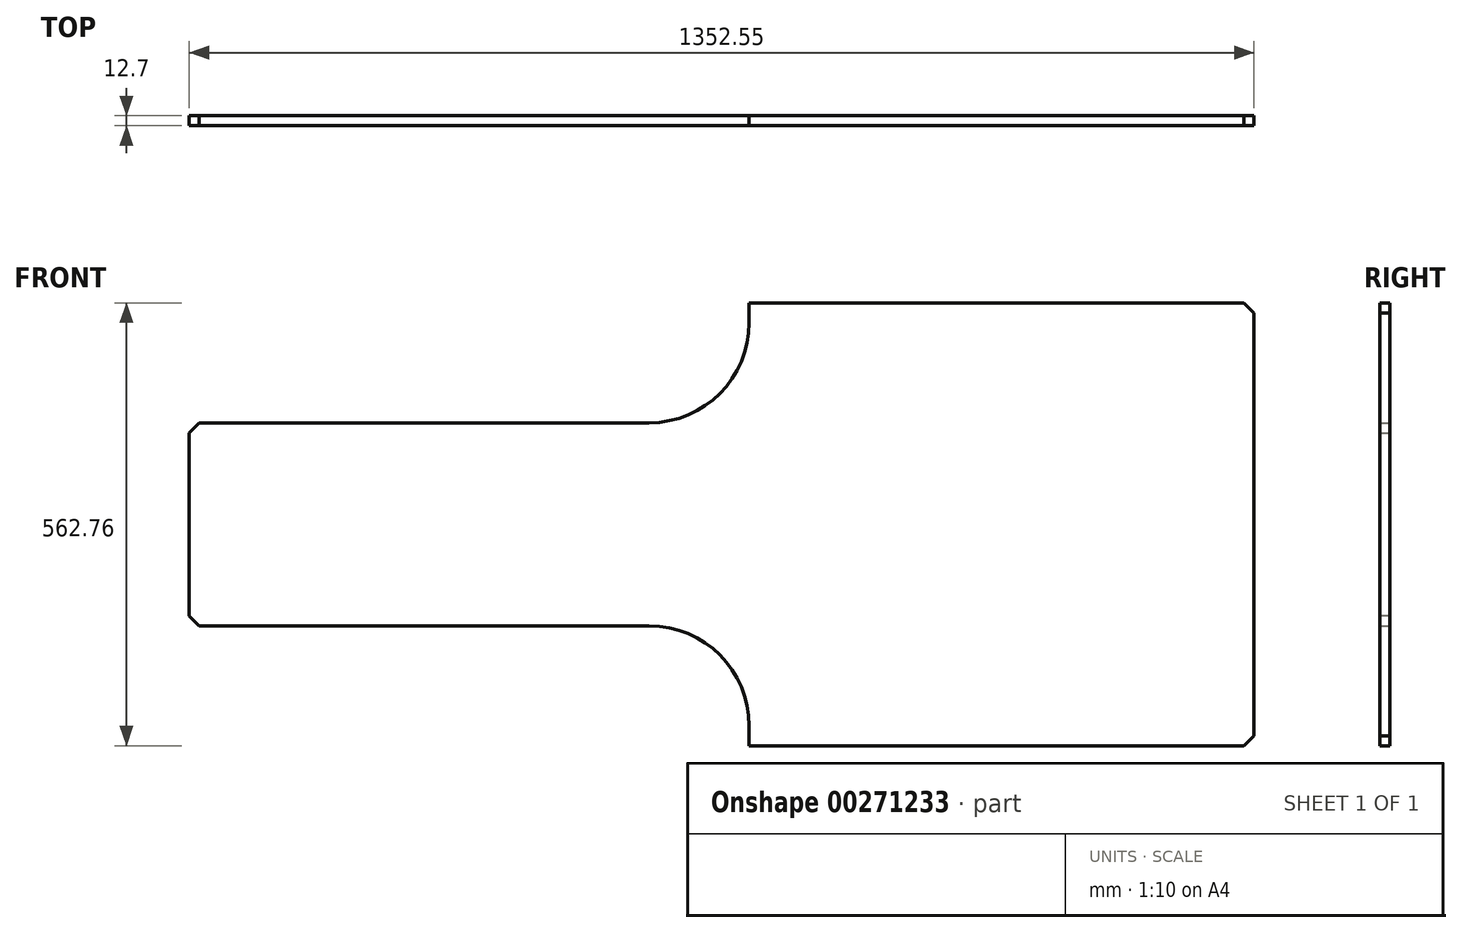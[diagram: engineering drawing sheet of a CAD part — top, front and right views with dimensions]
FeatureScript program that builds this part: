
annotation { "Feature Type Name" : "Feature", "Feature Type Description" : "" }
export const myFeature = defineFeature(function(context is Context, id is Id, definition is map)
    precondition{}
    {
        {
            var Q0;
            Q0=qCreatedBy(makeId("Front.planeOp"),FACE);
            var sketch = newSketch(context, id + "F0", { "sketchPlane" : qUnion([Q0])});
            skLineSegment(sketch, "E0.bottom", {"start": v(399.45, 149.86) * mm, "end": v(-241.9, 149.86) * mm});
            skLineSegment(sketch, "E0.top", {"start": v(399.45, -412.9) * mm, "end": v(-241.9, -412.9) * mm});
            skLineSegment(sketch, "E0.left", {"start": v(399.45, 149.86) * mm, "end": v(399.45, -412.9) * mm});
            skLineSegment(sketch, "E0.right", {"start": v(-953.1, -2.54) * mm, "end": v(-953.1, -260.5) * mm});
            skLineSegment(sketch, "E1", {"start": v(-241.9, 149.86) * mm, "end": v(-241.9, 124.46) * mm});
            skLineSegment(sketch, "E2", {"start": v(-953.1, -2.54) * mm, "end": v(-368.9, -2.54) * mm});
            skLineSegment(sketch, "E3", {"start": v(-953.1, -260.5) * mm, "end": v(-368.9, -260.5) * mm});
            skLineSegment(sketch, "E4.trimOffspring", {"start": v(-241.9, -387.5) * mm, "end": v(-241.9, -412.9) * mm});
            skPoint(sketch, "E5.visualSharp", {"position": v(-241.9, -2.54) * mm});
            skArc(sketch, "E5.filletArc", {"start": v(-368.9, -2.54) * mm, "mid": v(-279.1, 34.66) * mm, "end": v(-241.9, 124.46) * mm});
            skPoint(sketch, "E6.visualSharp", {"position": v(-241.9, -260.5) * mm});
            skArc(sketch, "E6.filletArc", {"start": v(-241.9, -387.5) * mm, "mid": v(-279.1, -297.7) * mm, "end": v(-368.9, -260.5) * mm});
            skSolve(sketch);
        }
        {
            var Q0;
            Q0 = qSketchRegion(id + "F0", true);
            extrude(context, id + "F1", {"entities" : qUnion([Q0]), "depth" : 12.7 * mm});
        }
        {
            var Q0;
            Q0=makeQuery(id+"F1.opExtrude","SWEPT_EDGE",EDGE,{"disambiguationData":[OSD([sQuery(id+"F0.wireOp",EDGE,"E0.right"),sQuery(id+"F0.wireOp",EDGE,"E2")])]});
            var Q1;
            Q1=makeQuery(id+"F1.opExtrude","SWEPT_EDGE",EDGE,{"disambiguationData":[OSD([sQuery(id+"F0.wireOp",EDGE,"E0.right"),sQuery(id+"F0.wireOp",EDGE,"E3")])]});
            var Q2;
            Q2=makeQuery(id+"F1.opExtrude","SWEPT_EDGE",EDGE,{"disambiguationData":[OSD([sQuery(id+"F0.wireOp",EDGE,"E0.top"),sQuery(id+"F0.wireOp",EDGE,"E0.left")])]});
            var Q3;
            Q3=makeQuery(id+"F1.opExtrude","SWEPT_EDGE",EDGE,{"disambiguationData":[OSD([sQuery(id+"F0.wireOp",EDGE,"E0.bottom"),sQuery(id+"F0.wireOp",EDGE,"E0.left")])]});
            chamfer(context, id + "F2", {"entities" : qUnion([Q0, Q1, Q2, Q3]), "width" : 12.7 * mm, "tangentPropagation" : true});
        }
    });
